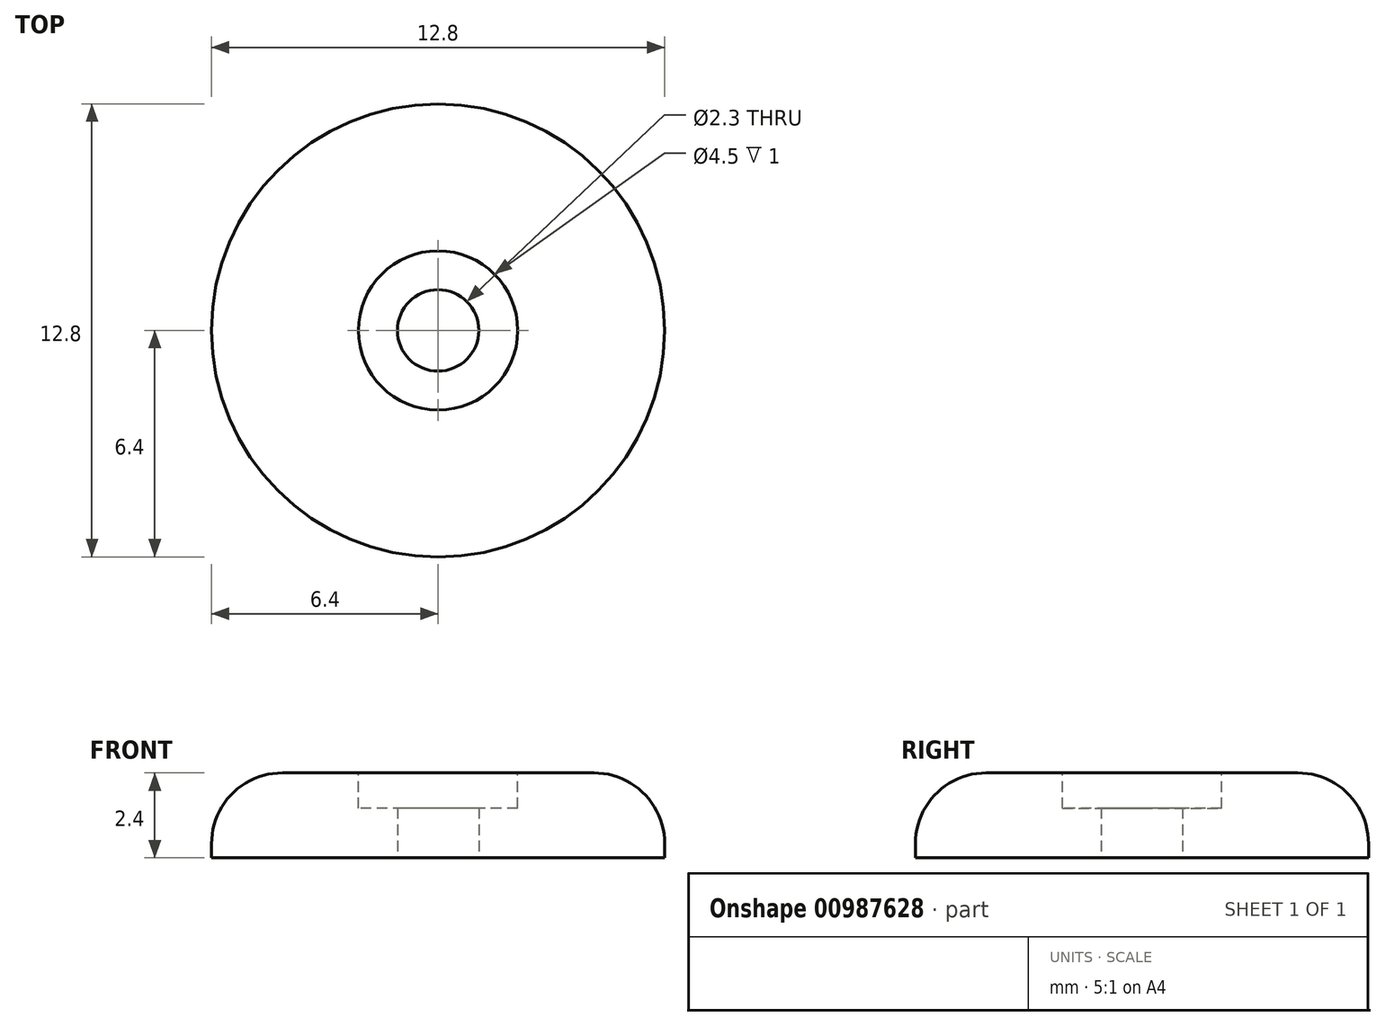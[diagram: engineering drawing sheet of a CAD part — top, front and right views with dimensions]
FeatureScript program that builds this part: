
annotation { "Feature Type Name" : "Feature", "Feature Type Description" : "" }
export const myFeature = defineFeature(function(context is Context, id is Id, definition is map)
    precondition{}
    {
        {
            var Q0;
            Q0=qCreatedBy(makeId("Top.planeOp"),FACE);
            var sketch = newSketch(context, id + "F0", { "sketchPlane" : qUnion([Q0])});
            skCircle(sketch, "E0", {"center": v(0, 0) * mm, "radius": 6.4 * mm});
            skCircle(sketch, "E1", {"center": v(0, 0) * mm, "radius": 1.15 * mm});
            skSolve(sketch);
        }
        {
            var Q0;
            Q0 = qSketchRegion(id + "F0", true);
            extrude(context, id + "F1", {"entities" : qUnion([Q0]), "depth" : 2.4 * mm, "offsetDistance" : 25 * mm});
        }
        {
            var Q0;
            Q0=makeQuery(id+"F1.opExtrude","CAP_FACE",FACE,{"disambiguationData":[OSD([sQuery(id+"F0.wireOp",EDGE,"E0"),sQuery(id+"F0.wireOp",EDGE,"E1")])],"isStart":false});
            var sketch = newSketch(context, id + "F2", { "sketchPlane" : qUnion([Q0])});
            skCircle(sketch, "E2", {"center": v(0, 0) * mm, "radius": 2.25 * mm});
            skSolve(sketch);
        }
        {
            var Q0;
            Q0 = qSketchRegion(id + "F2", true);
            extrude(context, id + "F3", {"entities" : qUnion([Q0]), "operationType" : NewBodyOperationType.REMOVE, "oppositeDirection" : true, "depth" : 1 * mm, "offsetDistance" : 25 * mm});
        }
        {
            var Q0;
            Q0=makeQuery(id+"F1.opExtrude","CAP_EDGE",EDGE,{"disambiguationData":[OSD([sQuery(id+"F0.wireOp",EDGE,"E0")])],"isStart":false});
            fillet(context, id + "F4", {"entities" : qUnion([Q0]), "radius" : 2 * mm, "tangentPropagation" : true, "allowEdgeOverflow" : false});
        }
    });
